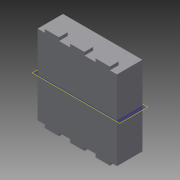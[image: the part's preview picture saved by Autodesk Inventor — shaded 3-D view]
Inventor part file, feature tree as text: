
AUTODESK INVENTOR PART (.ipt)
format: ipt  version: 2014 (Build 180170000, 170)  size: 131,584 bytes
history: native  units: mm
features: extrude x3, sketch x3, plane x1, mirror x1, fillet x1
ambient origin geometry x8: Origin, YZ Plane, XZ Plane, XY Plane, X Axis, Y Axis, Z Axis, Center Point
bodies: Volumenkörper1 (feature_tree)
feature tree (9):
  extrude  "Extrusion1"  Depth=5.0mm
  plane  "Arbeitsebene1"
  extrude  "Extrusion2"  Depth=0.9mm
  mirror  "Spiegeln1"
  extrude  "Extrusion3"  Depth=0.9mm
  fillet  "Rundung1"  Radius=0.7mm
  sketch  "Skizze1"  dims[d0=5.0mm d1=5.0mm]
  sketch  "Skizze2"  dims[d2=1.6mm d3=0.0mm d4=0.9mm]
  sketch  "Skizze3"  dims[d5=0.9mm d6=0.9mm d7=0.7mm d8=0.7mm d9=0.2mm d10=0.0mm d11=4.0mm d12=0.2mm d13=0.0mm d14=2.0mm]
